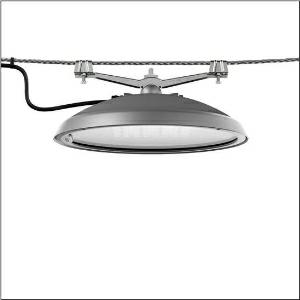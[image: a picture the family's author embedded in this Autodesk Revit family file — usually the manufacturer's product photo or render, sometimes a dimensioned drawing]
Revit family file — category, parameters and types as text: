
# Revit family: dl_r__50_iq_mini___st1_0s_5xa248w41f08he_3a14
name_source: partatom
category: Lighting Fixtures
units: mm (PartAtom-declared; Revit-internal decimal feet)

## family parameters
Cut with Voids When Loaded = No
Host = Face
Light Source = No
Part Type = Normal
Room Calculation Point = No
Round Connector Dimension = Use Diameter
Shared = No

## types (1)
- --- (1 x LED, 9400 lm, 64.6 W, 4000K)
    Apparent Load = 65 VA
    CIE Flux Codes = 37 72 97 100 100
    Color Rendering = 70
    Color Temperature = 4000K
    Default Elevation = 1800 mm
    Description = DL® 50 iQ mini, catenary luminaire, primary light control with lens, of PMMA, primary optical cover: cover, of toughened safety glass, transparent, light distribution: ST1.0s, light emission: direct distribution, primary light characteristic: symmetric, installation type: suspended mounting, LED, High Power LED, rated luminous flux: 9.400lm, luminous efficacy: 146lm/W, light colour: 740, colour temperature: 4000K, control gear: iQ Street-Remote, control: optimised constant luminous flux control (CLO 2.0), Desk-Remote (wireless, voltage-free reading and setting of iQ features in the workshop via application-optimized NFC function/RFID function), Light-Fading, Smart-Wire, Night-Set, Lumen-Switch, Temp-Guard, Auto-Match, Street-Remote, mains connection: 230..240V, AC, 50/60Hz, start of lifetime: 65W, end of service life: 68W, reduction: 29W, luminaire housing, of diecast aluminium, powder-coated, Siteco® metallic grey (DB 702S), diameter: 500mm, height: 115mm, mounting height: 4..12m, protection rating (complete): IP66, insulation class (complete): insulation class II (safety insulation), certification: CE, ENEC, ENEC+, VDE, impact resistance: IK08, permissible operating ambient temperature for outdoor applications: -25..+40°C, standard-compliant lighting for roads and squares, packaging unit: 1 piece

Light Distribution: ST1.0s
    Height = 124 mm  [stored 0.406824 ft]
    Lamp = 1 x LED
    Lamp Light Flux = 9400 lm
    Lamp Power = 64.6 W
    Lamp count = 1
    Length = 500 mm
    Luminous efficacy = 146 lm/W
    Manufacturer = Siteco
    ModVariant = No
    Model = 5XA248W41F08HE
    Number of Poles = 1
    OnlyDefault = Yes
    Power Factor = 1
    Product Name = DL® 50 iQ mini | ST1.0s
    Product group = catenary luminaire
    ProductGroupID = 6300
    Protection Class = Protection class II
    Protection Degree = IP 66
    RLX_Detail_Level = 1
    RLX_Emergency_Light_Flux = 0 lm
    RLX_Emergency_Type = 0
    RLX_Emergency_Type_DB = No
    RlxData = <blob elided: 123505 chars, md5=a1e0bd0a>
    Socket = socket
    Standby Power = 0 W
    System Light Flux = 9400 lm
    System Power = 65 W
    Type Comments = factory setting: luminous flux: 100 % | dim-lin: 254 | 655 mA
    Type Image = l_1242791.jpg
    URL = http://relux.com
    VarID = @adj_162081
    Voltage = 0 V
    Weight = 0.00 kg
    Width = 0 mm  [stored 0 ft]

note: [stored X ft] marks values corroborated as IEEE doubles in the binary element streams (Revit-internal decimal feet)

## geometry (parser evidence)
native form markers: Blend x4, Sweep x14
no freeform markers — native parametric forms only
